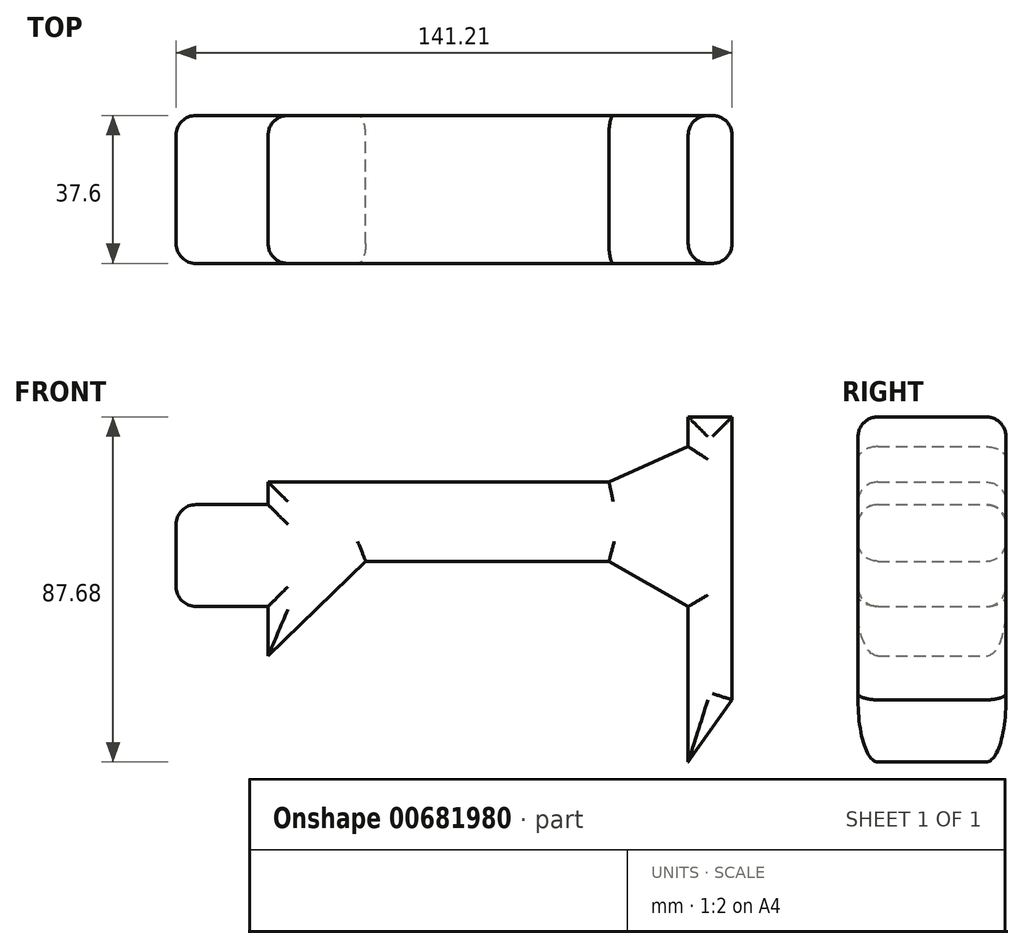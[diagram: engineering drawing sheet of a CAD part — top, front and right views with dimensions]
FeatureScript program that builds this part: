
annotation { "Feature Type Name" : "Feature", "Feature Type Description" : "" }
export const myFeature = defineFeature(function(context is Context, id is Id, definition is map)
    precondition{}
    {
        {
            var Q0;
            Q0=qCreatedBy(makeId("Front.planeOp"),FACE);
            var sketch = newSketch(context, id + "F0", { "sketchPlane" : qUnion([Q0])});
            skLineSegment(sketch, "E0", {"start": v(-123.06, 11.5) * mm, "end": v(-123.06, -14.37) * mm});
            skLineSegment(sketch, "E1", {"start": v(-123.06, -14.37) * mm, "end": v(-99.7, -14.37) * mm});
            skLineSegment(sketch, "E2", {"start": v(-99.7, -14.37) * mm, "end": v(-99.7, 11.5) * mm});
            skLineSegment(sketch, "E3", {"start": v(-99.7, 11.5) * mm, "end": v(-123.06, 11.5) * mm});
            skLineSegment(sketch, "E4", {"start": v(-99.7, 11.5) * mm, "end": v(-99.7, 17.25) * mm});
            skLineSegment(sketch, "E5", {"start": v(-99.7, 17.25) * mm, "end": v(-13.11, 17.25) * mm});
            skLineSegment(sketch, "E6", {"start": v(-13.11, 17.25) * mm, "end": v(7, 26.23) * mm});
            skLineSegment(sketch, "E7", {"start": v(7, 26.23) * mm, "end": v(7, 33.78) * mm});
            skLineSegment(sketch, "E8", {"start": v(7, 33.78) * mm, "end": v(18.15, 33.78) * mm});
            skLineSegment(sketch, "E9", {"start": v(18.15, 33.78) * mm, "end": v(18.15, -38.09) * mm});
            skLineSegment(sketch, "E10", {"start": v(18.15, -38.09) * mm, "end": v(7, -53.9) * mm});
            skPoint(sketch, "E10.endSnap0", {"position": v(7, 30) * mm});
            skLineSegment(sketch, "E11", {"start": v(7, -53.9) * mm, "end": v(7, -14.37) * mm});
            skLineSegment(sketch, "E12", {"start": v(7, -14.37) * mm, "end": v(-13.11, -2.87) * mm});
            skLineSegment(sketch, "E13", {"start": v(-13.11, -2.87) * mm, "end": v(-74.92, -2.87) * mm});
            skLineSegment(sketch, "E14", {"start": v(-74.92, -2.87) * mm, "end": v(-99.7, -26.95) * mm});
            skLineSegment(sketch, "E15", {"start": v(-99.7, -26.95) * mm, "end": v(-99.7, -14.37) * mm});
            skSolve(sketch);
        }
        {
            var Q0;
            Q0 = qSketchRegion(id + "F0", true);
            extrude(context, id + "F1", {"entities" : qUnion([Q0]), "depth" : 37.6 * mm, "offsetDistance" : 25 * mm});
        }
        {
            var Q0;
            Q0=makeQuery(id+"F1.opExtrude","CAP_FACE",FACE,{"disambiguationData":[OSD([sQuery(id+"F0.wireOp",EDGE,"E0"),sQuery(id+"F0.wireOp",EDGE,"E1"),sQuery(id+"F0.wireOp",EDGE,"E3"),sQuery(id+"F0.wireOp",EDGE,"E4"),sQuery(id+"F0.wireOp",EDGE,"E5"),sQuery(id+"F0.wireOp",EDGE,"E6"),sQuery(id+"F0.wireOp",EDGE,"E7"),sQuery(id+"F0.wireOp",EDGE,"E8"),sQuery(id+"F0.wireOp",EDGE,"E9"),sQuery(id+"F0.wireOp",EDGE,"E10"),sQuery(id+"F0.wireOp",EDGE,"E11"),sQuery(id+"F0.wireOp",EDGE,"E12"),sQuery(id+"F0.wireOp",EDGE,"E13"),sQuery(id+"F0.wireOp",EDGE,"E14"),sQuery(id+"F0.wireOp",EDGE,"E15")])],"isStart":false});
            var Q1;
            Q1=makeQuery(id+"F1.opExtrude","CAP_FACE",FACE,{"disambiguationData":[OSD([sQuery(id+"F0.wireOp",EDGE,"E0"),sQuery(id+"F0.wireOp",EDGE,"E1"),sQuery(id+"F0.wireOp",EDGE,"E3"),sQuery(id+"F0.wireOp",EDGE,"E4"),sQuery(id+"F0.wireOp",EDGE,"E5"),sQuery(id+"F0.wireOp",EDGE,"E6"),sQuery(id+"F0.wireOp",EDGE,"E7"),sQuery(id+"F0.wireOp",EDGE,"E8"),sQuery(id+"F0.wireOp",EDGE,"E9"),sQuery(id+"F0.wireOp",EDGE,"E10"),sQuery(id+"F0.wireOp",EDGE,"E11"),sQuery(id+"F0.wireOp",EDGE,"E12"),sQuery(id+"F0.wireOp",EDGE,"E13"),sQuery(id+"F0.wireOp",EDGE,"E14"),sQuery(id+"F0.wireOp",EDGE,"E15")])],"isStart":true});
            var Q2;
            Q2=makeQuery(id+"F1.opExtrude","SWEPT_FACE",FACE,{"disambiguationData":[OSD([sQuery(id+"F0.wireOp",EDGE,"E0")])]});
            fillet(context, id + "F2", {"entities" : qUnion([Q0, Q1, Q2]), "radius" : 5 * mm, "tangentPropagation" : true, "allowEdgeOverflow" : false});
        }
    });
